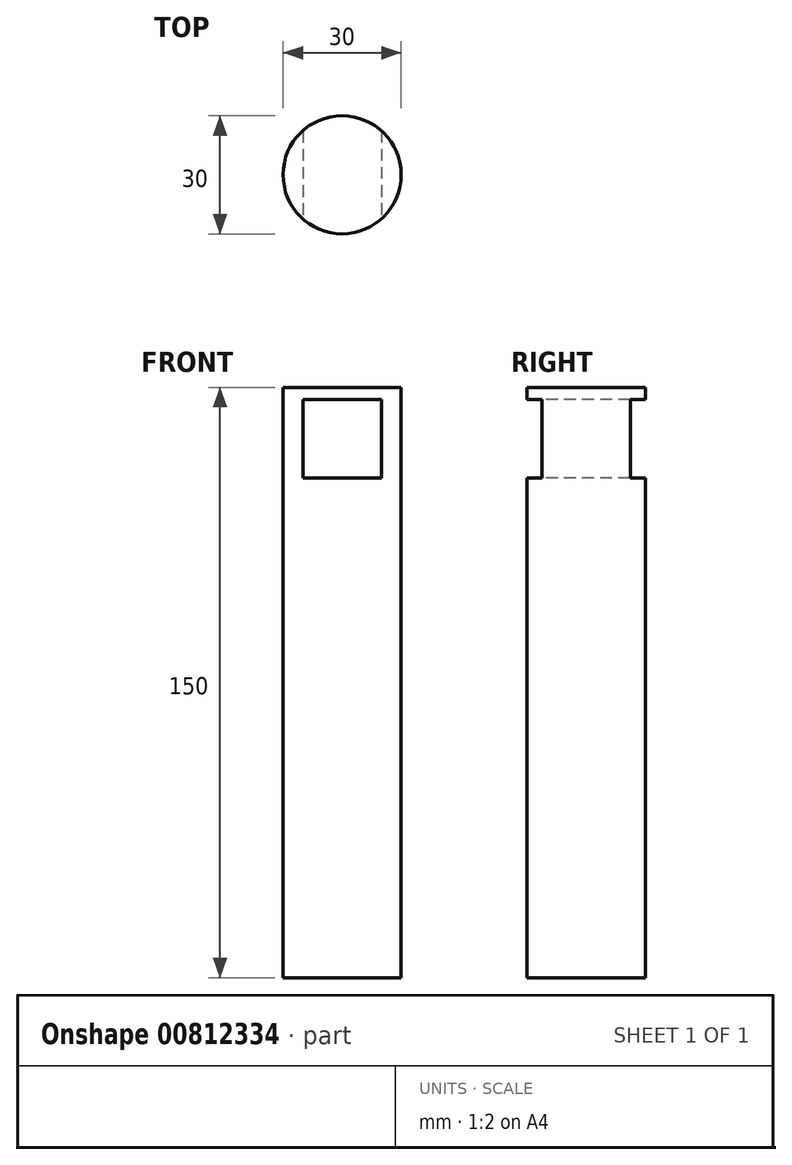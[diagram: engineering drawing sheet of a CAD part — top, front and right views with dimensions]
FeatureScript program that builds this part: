
annotation { "Feature Type Name" : "Feature", "Feature Type Description" : "" }
export const myFeature = defineFeature(function(context is Context, id is Id, definition is map)
    precondition{}
    {
        {
            var Q0;
            Q0=qCreatedBy(makeId("Top.planeOp"),FACE);
            var sketch = newSketch(context, id + "F0", { "sketchPlane" : qUnion([Q0])});
            skCircle(sketch, "E0", {"center": v(0, 0) * mm, "radius": 15 * mm});
            skSolve(sketch);
        }
        {
            var Q0;
            Q0=makeQuery(id+"F0.imprint","IMPRINT",FACE,{"disambiguationData":[TD([[makeQuery(id+"F0.imprint","IMPRINT",EDGE,{"derivedFrom":sQuery(id+"F0.wireOp",EDGE,"E0")}),1.0]])]});
            extrude(context, id + "F1", {"entities" : qUnion([Q0]), "depth" : 150 * mm, "offsetDistance" : 25 * mm});
        }
        {
            var Q0;
            Q0=qCreatedBy(makeId("Front.planeOp"),FACE);
            var sketch = newSketch(context, id + "F2", { "sketchPlane" : qUnion([Q0])});
            skLineSegment(sketch, "E1.bottom", {"start": v(-10, 146.91) * mm, "end": v(10, 146.91) * mm});
            skLineSegment(sketch, "E1.top", {"start": v(-10, 126.91) * mm, "end": v(10, 126.91) * mm});
            skLineSegment(sketch, "E1.left", {"start": v(-10, 146.91) * mm, "end": v(-10, 126.91) * mm});
            skLineSegment(sketch, "E1.right", {"start": v(10, 146.91) * mm, "end": v(10, 126.91) * mm});
            skSolve(sketch);
        }
        {
            var Q0;
            Q0 = qSketchRegion(id + "F2", true);
            extrude(context, id + "F3", {"entities" : qUnion([Q0]), "operationType" : NewBodyOperationType.REMOVE, "endBound" : BoundingType.UP_TO_NEXT, "oppositeDirection" : true, "depth" : 25 * mm, "offsetDistance" : 25 * mm, "hasSecondDirection" : true, "secondDirectionBound" : SecondDirectionBoundingType.UP_TO_NEXT, "secondDirectionOppositeDirection" : false, "secondDirectionDepth" : 25 * mm});
        }
    });
